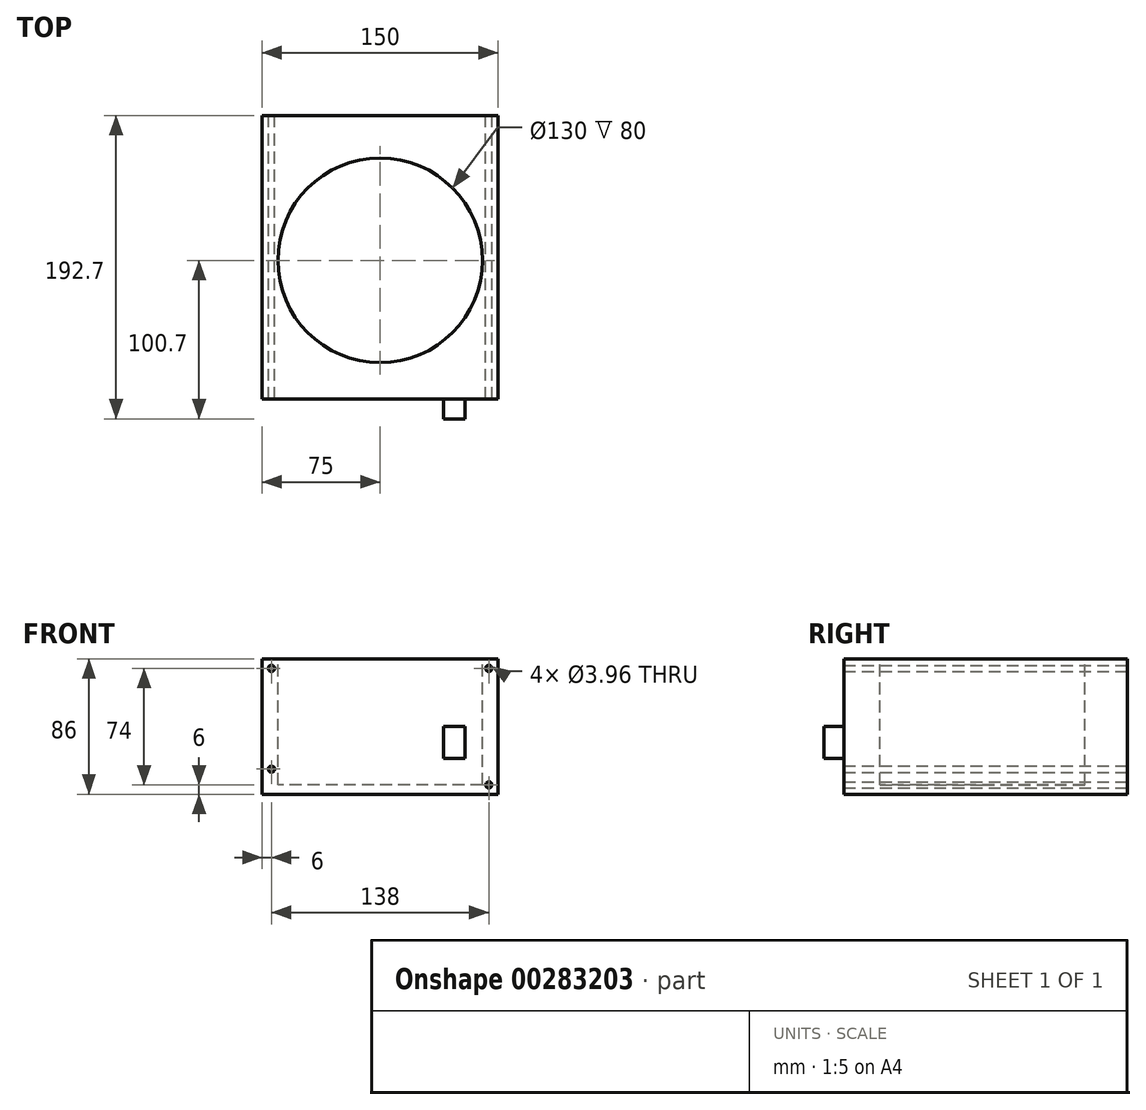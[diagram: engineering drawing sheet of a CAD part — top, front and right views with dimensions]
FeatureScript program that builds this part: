
annotation { "Feature Type Name" : "Feature", "Feature Type Description" : "" }
export const myFeature = defineFeature(function(context is Context, id is Id, definition is map)
    precondition{}
    {
        {
            var Q0;
            Q0=qCreatedBy(makeId("Front.planeOp"),FACE);
            var sketch = newSketch(context, id + "F0", { "sketchPlane" : qUnion([Q0])});
            skLineSegment(sketch, "E0.bottom", {"start": v(75, -43) * mm, "end": v(-75, -43) * mm});
            skLineSegment(sketch, "E0.top", {"start": v(75, 43) * mm, "end": v(-75, 43) * mm});
            skLineSegment(sketch, "E0.left", {"start": v(75, -43) * mm, "end": v(75, 43) * mm});
            skLineSegment(sketch, "E0.right", {"start": v(-75, -43) * mm, "end": v(-75, 43) * mm});
            skPoint(sketch, "E0.middle", {"position": v(0, 0) * mm});
            skLineSegment(sketch, "E1", {"start": v(-75, 43) * mm, "end": v(-69, 43) * mm, "construction": true});
            skLineSegment(sketch, "E2", {"start": v(-69, 43) * mm, "end": v(-69, 37) * mm, "construction": true});
            skLineSegment(sketch, "E3", {"start": v(-69, 37) * mm, "end": v(-69, -27) * mm, "construction": true});
            skLineSegment(sketch, "E4", {"start": v(-69, 37) * mm, "end": v(69, 37) * mm, "construction": true});
            skLineSegment(sketch, "E5", {"start": v(69, 37) * mm, "end": v(69, -37) * mm, "construction": true});
            skLineSegment(sketch, "E6", {"start": v(69, -37) * mm, "end": v(45, -37) * mm, "construction": true});
            skCircle(sketch, "E7", {"center": v(-69, 37) * mm, "radius": 1.98 * mm});
            skCircle(sketch, "E8", {"center": v(-69, -27) * mm, "radius": 1.98 * mm});
            skCircle(sketch, "E9", {"center": v(69, 37) * mm, "radius": 1.98 * mm});
            skCircle(sketch, "E10", {"center": v(69, -37) * mm, "radius": 1.98 * mm});
            skSolve(sketch);
        }
        {
            var Q0;
            Q0=makeQuery(id+"F0.imprint","IMPRINT",FACE,{"disambiguationData":[TD([[makeQuery(id+"F0.imprint","IMPRINT",EDGE,{"derivedFrom":sQuery(id+"F0.wireOp",EDGE,"E0.bottom")}),-1.0]])]});
            extrude(context, id + "F1", {"entities" : qUnion([Q0]), "depth" : 180 * mm});
        }
        {
            var Q0;
            Q0=makeQuery(id+"F1.opExtrude","SWEPT_FACE",FACE,{"disambiguationData":[OSD([sQuery(id+"F0.wireOp",EDGE,"E0.top")])]});
            var sketch = newSketch(context, id + "F2", { "sketchPlane" : qUnion([Q0])});
            skLineSegment(sketch, "E11", {"start": v(0, 0) * mm, "end": v(0, -27) * mm, "construction": true});
            skPoint(sketch, "E11.endSnap0", {"position": v(0, 0) * mm});
            skLineSegment(sketch, "E12", {"start": v(0, -27) * mm, "end": v(0, -157) * mm, "construction": true});
            skLineSegment(sketch, "E13", {"start": v(0, -157) * mm, "end": v(0, -180) * mm, "construction": true});
            skPoint(sketch, "E13.endSnap0", {"position": v(0, -180) * mm});
            skCircle(sketch, "E14", {"center": v(0, -92) * mm, "radius": 65 * mm});
            skSolve(sketch);
        }
        {
            var Q0;
            Q0 = qSketchRegion(id + "F2", true);
            extrude(context, id + "F3", {"entities" : qUnion([Q0]), "operationType" : NewBodyOperationType.REMOVE, "oppositeDirection" : true, "depth" : 80 * mm});
        }
        {
            var Q0;
            Q0=makeQuery(id+"F1.opExtrude","CAP_FACE",FACE,{"disambiguationData":[OSD([sQuery(id+"F0.wireOp",EDGE,"E0.bottom"),sQuery(id+"F0.wireOp",EDGE,"E0.top"),sQuery(id+"F0.wireOp",EDGE,"E0.left"),sQuery(id+"F0.wireOp",EDGE,"E0.right"),sQuery(id+"F0.wireOp",EDGE,"E7"),sQuery(id+"F0.wireOp",EDGE,"E8"),sQuery(id+"F0.wireOp",EDGE,"E9"),sQuery(id+"F0.wireOp",EDGE,"E10")])],"isStart":false});
            var sketch = newSketch(context, id + "F4", { "sketchPlane" : qUnion([Q0])});
            skLineSegment(sketch, "E15.bottom", {"start": v(40.3, 0) * mm, "end": v(54.02, 0) * mm});
            skLineSegment(sketch, "E15.top", {"start": v(40.3, -20.18) * mm, "end": v(54.02, -20.18) * mm});
            skLineSegment(sketch, "E15.left", {"start": v(40.3, 0) * mm, "end": v(40.3, -20.18) * mm});
            skLineSegment(sketch, "E15.right", {"start": v(54.02, 0) * mm, "end": v(54.02, -20.18) * mm});
            skSolve(sketch);
        }
        {
            var Q0;
            Q0 = qSketchRegion(id + "F4", true);
            extrude(context, id + "F5", {"entities" : qUnion([Q0]), "operationType" : NewBodyOperationType.ADD, "depth" : 12.7 * mm});
        }
    });
